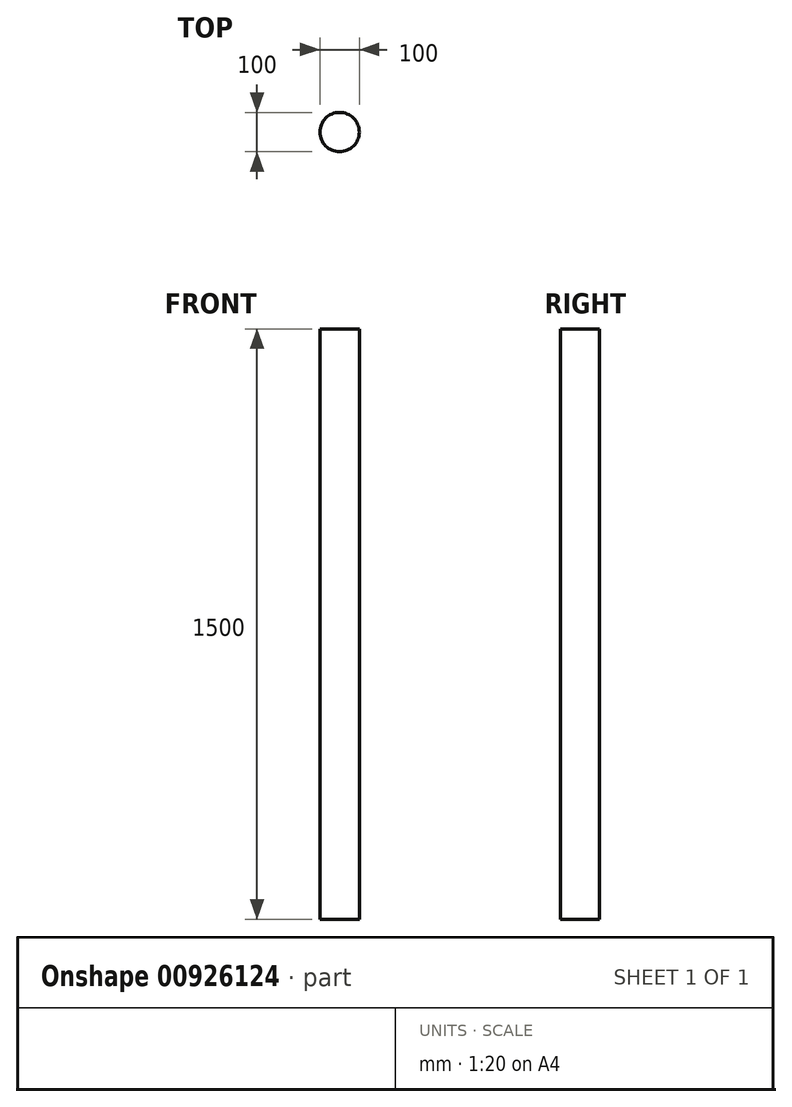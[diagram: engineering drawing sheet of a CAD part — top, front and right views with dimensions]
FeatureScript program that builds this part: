
annotation { "Feature Type Name" : "Feature", "Feature Type Description" : "" }
export const myFeature = defineFeature(function(context is Context, id is Id, definition is map)
    precondition{}
    {
        {
            var Q0;
            Q0=qCreatedBy(makeId("Top.planeOp"),FACE);
            var sketch = newSketch(context, id + "F0", { "sketchPlane" : qUnion([Q0])});
            skCircle(sketch, "E0", {"center": v(0, 0) * mm, "radius": 50 * mm});
            skSolve(sketch);
        }
        {
            var Q0;
            Q0 = qSketchRegion(id + "F0", true);
            extrude(context, id + "F1", {"entities" : qUnion([Q0]), "depth" : 1500 * mm, "offsetDistance" : 25 * mm});
        }
    });
